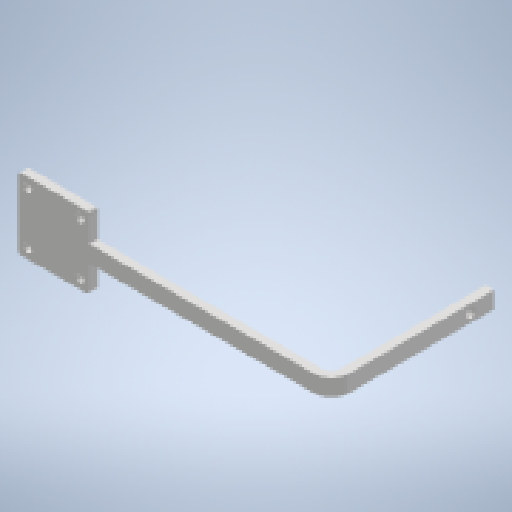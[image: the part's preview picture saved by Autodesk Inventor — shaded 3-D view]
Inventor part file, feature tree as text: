
AUTODESK INVENTOR PART (.ipt)
format: ipt  version: 2023 (Build 270158000, 158)  size: 192,512 bytes
history: native  units: mm
features: reference x15, other x5, sheet_metal_op x3, sketch x2
ambient origin geometry x8: Origin, YZ Plane, XZ Plane, XY Plane, X Axis, Y Axis, Z Axis, Center Point
bodies: Solid1 (feature_tree)
feature tree (25):
  sheet_metal_op  "Face1"
  sheet_metal_op  "Face2"
  sketch  "Sketch1"  dims[d0=2.0mm]
  reference  "Reference1"
  reference  "Reference2"
  reference  "Reference3"
  reference  "Reference4"
  reference  "Reference5"
  reference  "Reference6"
  reference  "Reference7"
  reference  "Reference8"
  reference  "Reference9"
  reference  "Reference10"
  reference  "Reference11"
  reference  "Reference12"
  other  "Plate1"
  sketch  "Sketch2"  dims[d1=5.0mm d2=5.0mm d3=5.0mm d4=2.5mm d5=10.0mm d6=5.0mm]
  reference  "Reference13"
  reference  "Reference14"
  reference  "Reference15"
  other  "Plate2"
  sheet_metal_op  "Bend1"
  other  "ensamble_general.iam"
  other  "stepper:1"
  other  "sostenedor_part1_MIR:1"
